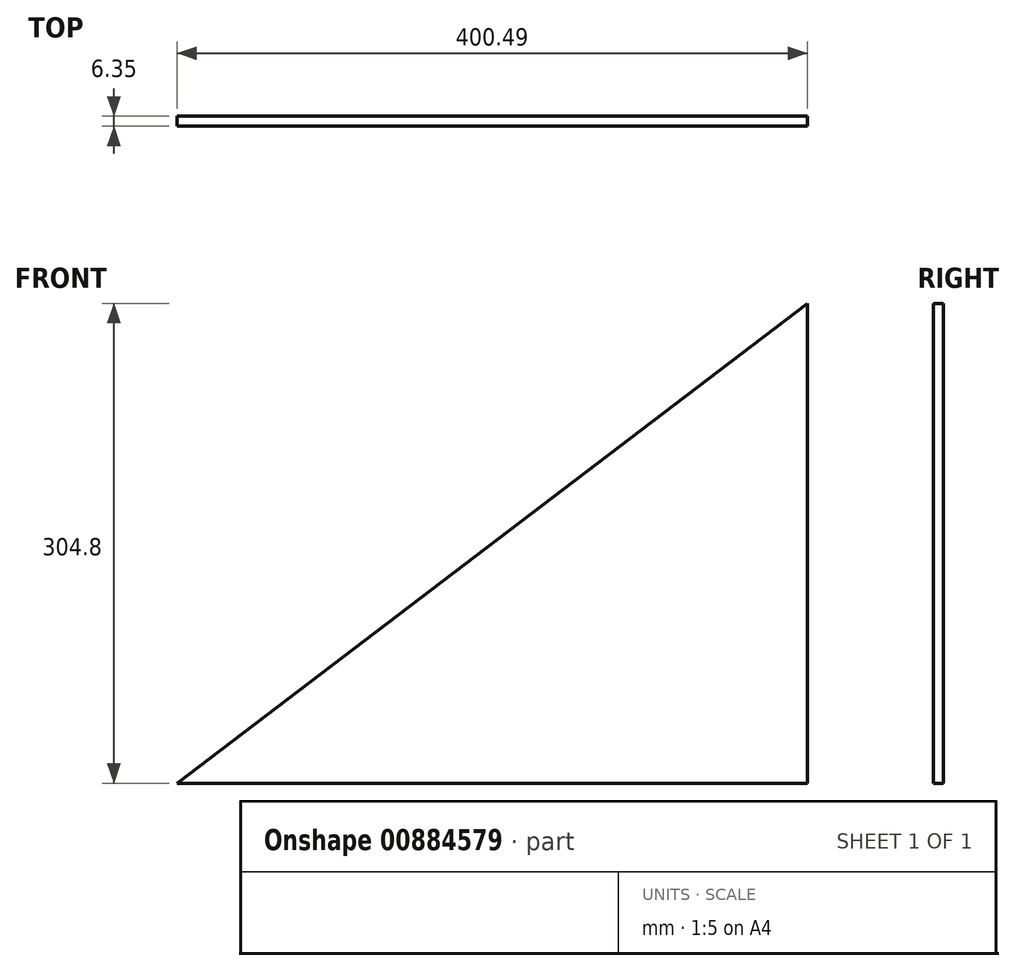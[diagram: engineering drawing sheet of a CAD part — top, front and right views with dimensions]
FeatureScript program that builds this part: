
annotation { "Feature Type Name" : "Feature", "Feature Type Description" : "" }
export const myFeature = defineFeature(function(context is Context, id is Id, definition is map)
    precondition{}
    {
        {
            var Q0;
            Q0=qCreatedBy(makeId("Front.planeOp"),FACE);
            var sketch = newSketch(context, id + "F0", { "sketchPlane" : qUnion([Q0])});
            skLineSegment(sketch, "E0", {"start": v(-400.49, 0) * mm, "end": v(0, 304.8) * mm});
            skLineSegment(sketch, "E1", {"start": v(0, 304.8) * mm, "end": v(0, 0) * mm});
            skLineSegment(sketch, "E2", {"start": v(0, 0) * mm, "end": v(-400.49, 0) * mm});
            skSolve(sketch);
        }
        {
            var Q0;
            Q0=makeQuery(id+"F0.imprint","IMPRINT",FACE,{"disambiguationData":[TD([[makeQuery(id+"F0.imprint","IMPRINT",EDGE,{"derivedFrom":sQuery(id+"F0.wireOp",EDGE,"E0")}),-1.0]])]});
            var sketch = newSketch(context, id + "F1", { "sketchPlane" : qUnion([Q0])});
            skSolve(sketch);
        }
        {
            var Q0;
            Q0=makeQuery(id+"F1.imprint","IMPRINT",FACE,{"disambiguationData":[TD([[makeQuery(id+"F1.imprint","IMPRINT",EDGE,{"derivedFrom":makeQuery(id+"F0.imprint","IMPRINT",EDGE,{"derivedFrom":sQuery(id+"F0.wireOp",EDGE,"E0")})}),-1.0]])]});
            extrude(context, id + "F2", {"entities" : qUnion([Q0]), "depth" : 6.35 * mm, "offsetDistance" : 25.4 * mm});
        }
    });
